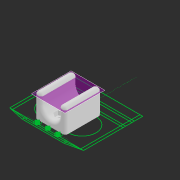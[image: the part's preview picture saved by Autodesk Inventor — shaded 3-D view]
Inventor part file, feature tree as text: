
AUTODESK INVENTOR PART (.ipt)
format: ipt  version: 2020.3 (Build 243373010, 373A)  size: 281,088 bytes
history: native  units: mm
features: fillet x5, extrude x4, sketch x3, other x1, plane x1, projected_geometry x1
ambient origin geometry x8: Origin, YZ Plane, XZ Plane, XY Plane, X Axis, Y Axis, Z Axis, Center Point
bodies: Solid1 (feature_tree)
feature tree (15):
  other  "body.ipt"
  sketch  "Sketch2"  dims[d2=22.0mm d3=5.8mm]
  extrude  "Extrusion1"  Depth=13.0mm
  extrude  "Extrusion2"  Depth=5.8mm
  extrude  "Extrusion3"  Depth=4.0mm TaperAngle=0.0deg
  fillet  "Fillet1"  Radius=15.0mm
  fillet  "Fillet2"  Radius=6.0mm
  fillet  "Fillet3"  Radius=6.0mm
  plane  "Work Plane1"
  extrude  "Extrusion4"  Depth=26.0mm TaperAngle=0.0deg
  fillet  "Fillet4"  Radius=2.3mm
  fillet  "Fillet5"  Radius=2.3mm
  sketch  "Sketch1"  dims[d0=10.0mm d1=13.0mm]
  sketch  "Sketch3"  dims[d4=5.8mm d5=4.0mm d6=0.0mm d7=15.0mm d8=0.0mm d9=6.0mm d10=6.0mm d11=26.0mm d12=0.0mm d13=2.3mm d14=2.3mm d15=2.0mm d16=2.0mm d17=2.0mm d18=-15.25mm d19=13.75mm d20=0.0mm d21=0.4mm d22=0.2mm]
  projected_geometry  "Projected Loop1"
